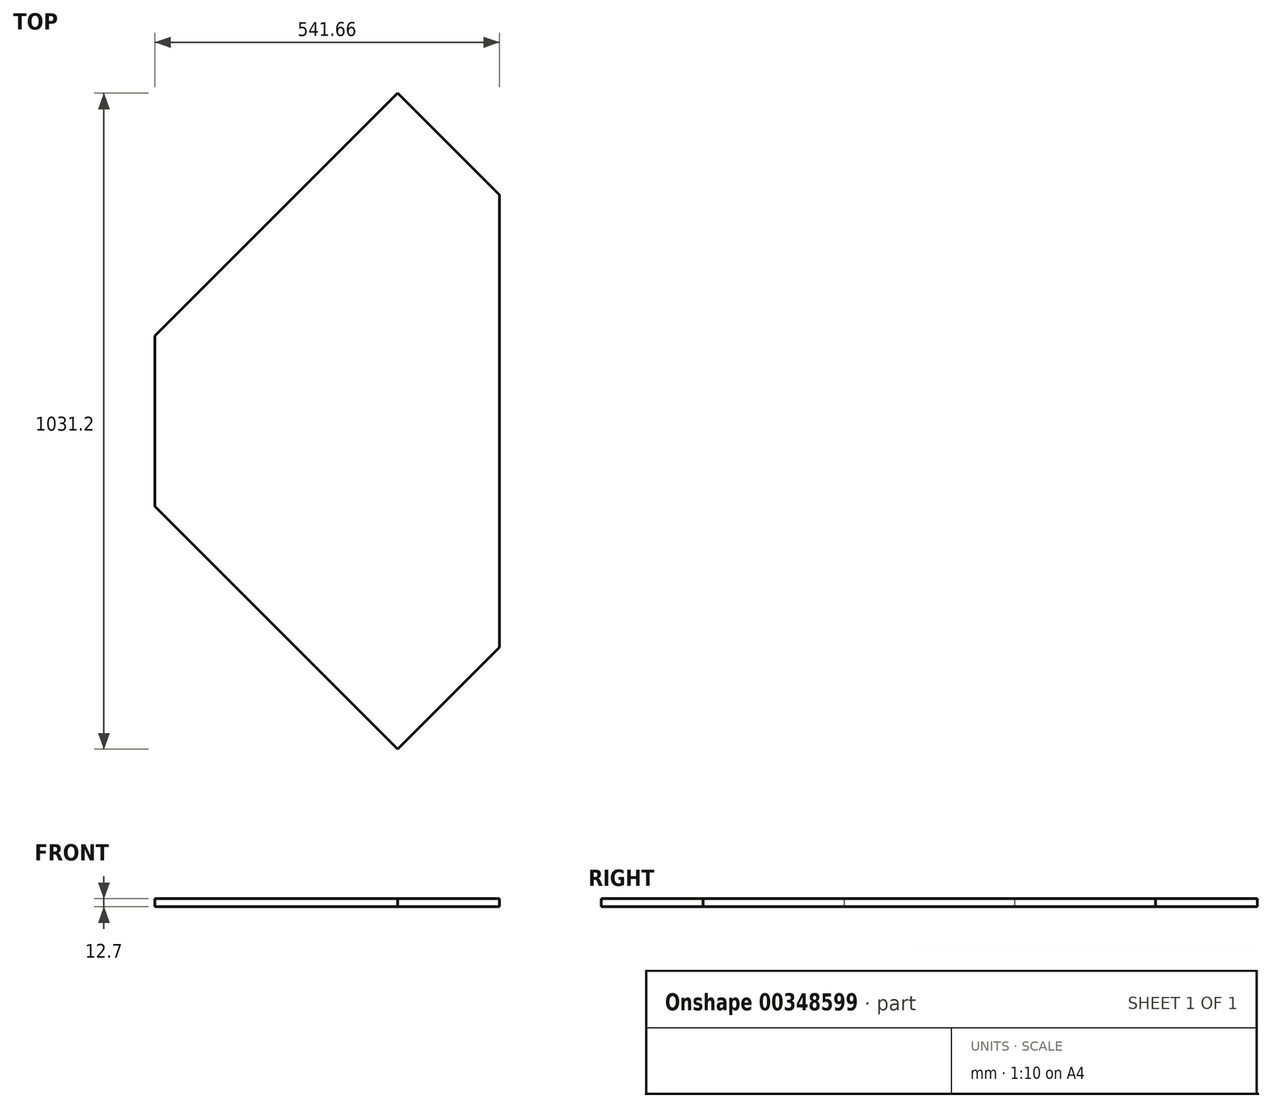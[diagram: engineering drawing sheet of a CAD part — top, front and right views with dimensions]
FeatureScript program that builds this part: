
annotation { "Feature Type Name" : "Feature", "Feature Type Description" : "" }
export const myFeature = defineFeature(function(context is Context, id is Id, definition is map)
    precondition{}
    {
        {
            var Q0;
            Q0=qCreatedBy(makeId("Top.planeOp"),FACE);
            var sketch = newSketch(context, id + "F0", { "sketchPlane" : qUnion([Q0])});
            skLineSegment(sketch, "E0.bottom", {"start": v(-399.28, 902.47) * mm, "end": v(-17.62, 1284.13) * mm});
            skLineSegment(sketch, "E1", {"start": v(-17.62, 1284.13) * mm, "end": v(-399.28, 902.47) * mm});
            skLineSegment(sketch, "E2", {"start": v(-399.28, 902.47) * mm, "end": v(-399.28, 634.6) * mm});
            skLineSegment(sketch, "E3", {"start": v(-399.28, 634.6) * mm, "end": v(-17.62, 252.93) * mm});
            skLineSegment(sketch, "E4", {"start": v(-17.62, 252.93) * mm, "end": v(142.38, 412.93) * mm});
            skLineSegment(sketch, "E5", {"start": v(142.38, 412.93) * mm, "end": v(142.38, 1124.13) * mm});
            skLineSegment(sketch, "E6", {"start": v(142.38, 1124.13) * mm, "end": v(-17.62, 1284.13) * mm});
            skSolve(sketch);
        }
        {
            var Q0;
            Q0=qSketchRegion(id+"F0",true);
            extrude(context, id + "F1", {"entities" : qUnion([Q0]), "depth" : 12.7 * mm});
        }
    });
